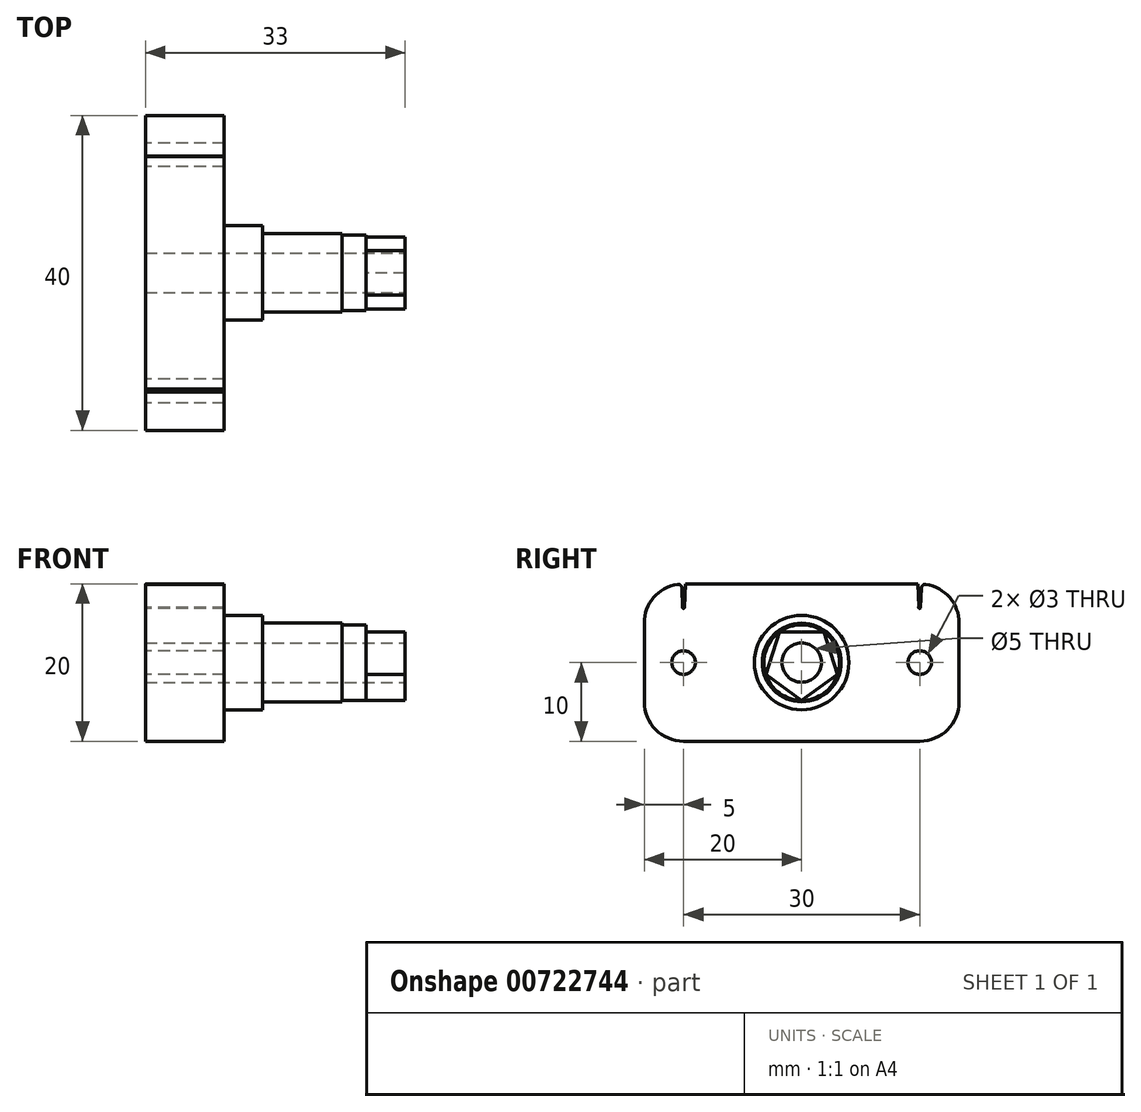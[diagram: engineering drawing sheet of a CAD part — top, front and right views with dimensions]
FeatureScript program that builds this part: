
annotation { "Feature Type Name" : "Feature", "Feature Type Description" : "" }
export const myFeature = defineFeature(function(context is Context, id is Id, definition is map)
    precondition{}
    {
        {
            var Q0;
            Q0=qCreatedBy(makeId("Right.planeOp"),FACE);
            var sketch = newSketch(context, id + "F0", { "sketchPlane" : qUnion([Q0])});
            skCircle(sketch, "E0", {"center": v(0, 0) * mm, "radius": 5 * mm});
            skSolve(sketch);
        }
        {
            var Q0;
            Q0=qSketchRegion(id+"F0",true);
            extrude(context, id + "F1", {"entities" : qUnion([Q0]), "oppositeDirection" : true, "depth" : 25 * mm, "offsetDistance" : 25 * mm});
        }
        {
            var Q0;
            Q0=makeQuery(id+"F1.opExtrude","CAP_FACE",FACE,{"disambiguationData":[OSD([sQuery(id+"F0.wireOp",EDGE,"E0")])],"isStart":true});
            var sketch = newSketch(context, id + "F2", { "sketchPlane" : qUnion([Q0])});
            skCircle(sketch, "E1", {"center": v(0, 0) * mm, "radius": 4.8 * mm});
            skSolve(sketch);
        }
        {
            var Q0;
            Q0=qSketchRegion(id+"F2",true);
            extrude(context, id + "F3", {"entities" : qUnion([Q0]), "operationType" : NewBodyOperationType.ADD, "depth" : 3 * mm, "offsetDistance" : 25 * mm});
        }
        {
            var Q0;
            Q0=makeQuery(id+"F3.opExtrude","CAP_FACE",FACE,{"disambiguationData":[OSD([sQuery(id+"F2.wireOp",EDGE,"E1")])],"isStart":false});
            var sketch = newSketch(context, id + "F4", { "sketchPlane" : qUnion([Q0])});
            skCircle(sketch, "E2.cCircle", {"center": v(0, 0) * mm, "radius": 4.8 * mm, "construction": true});
            skLineSegment(sketch, "E2.0", {"start": v(0, -4.8) * mm, "end": v(-4.57, -1.48) * mm});
            skLineSegment(sketch, "E2.1", {"start": v(-4.57, -1.48) * mm, "end": v(-2.82, 3.88) * mm});
            skLineSegment(sketch, "E2.2", {"start": v(-2.82, 3.88) * mm, "end": v(2.82, 3.88) * mm});
            skLineSegment(sketch, "E2.3", {"start": v(2.82, 3.88) * mm, "end": v(4.57, -1.48) * mm});
            skLineSegment(sketch, "E2.4", {"start": v(4.57, -1.48) * mm, "end": v(0, -4.8) * mm});
            skSolve(sketch);
        }
        {
            var Q0;
            Q0=qSketchRegion(id+"F4",true);
            extrude(context, id + "F5", {"entities" : qUnion([Q0]), "operationType" : NewBodyOperationType.ADD, "depth" : 5 * mm, "offsetDistance" : 25 * mm, "hasSecondDirection" : true, "secondDirectionOppositeDirection" : true, "secondDirectionDepth" : 23 * mm});
        }
        {
            var Q0;
            Q0=makeQuery(id+"F1.opExtrude","CAP_FACE",FACE,{"disambiguationData":[OSD([sQuery(id+"F0.wireOp",EDGE,"E0")])],"isStart":false});
            var sketch = newSketch(context, id + "F6", { "sketchPlane" : qUnion([Q0])});
            skLineSegment(sketch, "E3.bottom", {"start": v(-20, 10) * mm, "end": v(20, 10) * mm});
            skLineSegment(sketch, "E3.top", {"start": v(-20, -10) * mm, "end": v(20, -10) * mm});
            skLineSegment(sketch, "E3.left", {"start": v(-20, 10) * mm, "end": v(-20, -10) * mm});
            skLineSegment(sketch, "E3.right", {"start": v(20, 10) * mm, "end": v(20, -10) * mm});
            skPoint(sketch, "E3.middle", {"position": v(0, 0) * mm});
            skLineSegment(sketch, "E4", {"start": v(0, 0) * mm, "end": v(-15, 0) * mm, "construction": true});
            skLineSegment(sketch, "E5", {"start": v(0, 0) * mm, "end": v(15, 0) * mm});
            skCircle(sketch, "E6", {"center": v(-15, 0) * mm, "radius": 1.5 * mm});
            skCircle(sketch, "E7", {"center": v(15, 0) * mm, "radius": 1.5 * mm});
            skSolve(sketch);
        }
        {
            var Q0;
            Q0 = qSketchRegion(id + "F6", true);
            extrude(context, id + "F7", {"entities" : qUnion([Q0]), "operationType" : NewBodyOperationType.ADD, "oppositeDirection" : true, "depth" : 10 * mm, "offsetDistance" : 25 * mm});
        }
        {
            var Q0;
            Q0=makeQuery(id+"F7.boolean.opBoolean","MERGE",FACE,{"derivedFrom":[makeQuery(id+"F5.opExtrude","CAP_FACE",FACE,{"disambiguationData":[OSD([sQuery(id+"F4.wireOp",EDGE,"E2.0"),sQuery(id+"F4.wireOp",EDGE,"E2.1"),sQuery(id+"F4.wireOp",EDGE,"E2.2"),sQuery(id+"F4.wireOp",EDGE,"E2.3"),sQuery(id+"F4.wireOp",EDGE,"E2.4")])],"isStart":true}),makeQuery(id+"F7.opExtrude","CAP_FACE",FACE,{"disambiguationData":[OSD([sQuery(id+"F6.wireOp",EDGE,"E3.bottom"),sQuery(id+"F6.wireOp",EDGE,"E3.top"),sQuery(id+"F6.wireOp",EDGE,"E3.left"),sQuery(id+"F6.wireOp",EDGE,"E3.right"),sQuery(id+"F6.wireOp",EDGE,"E6"),sQuery(id+"F6.wireOp",EDGE,"E7")])],"isStart":true})]});
            var sketch = newSketch(context, id + "F8", { "sketchPlane" : qUnion([Q0])});
            skLineSegment(sketch, "E8", {"start": v(0, 10) * mm, "end": v(-14.8, 10) * mm, "construction": true});
            skLineSegment(sketch, "E9", {"start": v(-15, 10) * mm, "end": v(-15, 7) * mm, "construction": true});
            skLineSegment(sketch, "E10", {"start": v(-14.8, 10) * mm, "end": v(-15, 10) * mm});
            skLineSegment(sketch, "E11", {"start": v(-15, 10) * mm, "end": v(-14.8, 10) * mm});
            skLineSegment(sketch, "E12", {"start": v(0, 10) * mm, "end": v(15, 10) * mm, "construction": true});
            skLineSegment(sketch, "E13", {"start": v(15, 10) * mm, "end": v(15, 7) * mm, "construction": true});
            skLineSegment(sketch, "E14", {"start": v(14.99, 10) * mm, "end": v(14.74, 10) * mm});
            skLineSegment(sketch, "E15", {"start": v(15.24, 10) * mm, "end": v(15.05, 10) * mm});
            skLineSegment(sketch, "E16", {"start": v(14.99, 10) * mm, "end": v(15.24, 10) * mm});
            skArc(sketch, "E17", {"start": v(14.88, 7) * mm, "mid": v(15.02, 6.88) * mm, "end": v(15.12, 7.03) * mm});
            skLineSegment(sketch, "E18", {"start": v(15.12, 7.03) * mm, "end": v(15.24, 10) * mm});
            skLineSegment(sketch, "E19", {"start": v(14.74, 10) * mm, "end": v(14.88, 7) * mm});
            skLineSegment(sketch, "E20", {"start": v(15.24, 10) * mm, "end": v(14.74, 10) * mm});
            skLineSegment(sketch, "E21", {"start": v(-12.57, 9.9) * mm, "end": v(-12.57, 6.9) * mm, "construction": true});
            skLineSegment(sketch, "E22", {"start": v(-15, 10) * mm, "end": v(-15.25, 10) * mm});
            skLineSegment(sketch, "E23", {"start": v(-14.75, 10) * mm, "end": v(-14.94, 10) * mm});
            skLineSegment(sketch, "E24", {"start": v(-15, 10) * mm, "end": v(-14.75, 10) * mm});
            skArc(sketch, "E25", {"start": v(-15.11, 7) * mm, "mid": v(-14.97, 6.88) * mm, "end": v(-14.86, 7.03) * mm});
            skLineSegment(sketch, "E26", {"start": v(-14.86, 7.03) * mm, "end": v(-14.75, 10) * mm});
            skLineSegment(sketch, "E27", {"start": v(-15.25, 10) * mm, "end": v(-15.11, 7) * mm});
            skLineSegment(sketch, "E28", {"start": v(-14.75, 10) * mm, "end": v(-15.25, 10) * mm});
            skSolve(sketch);
        }
        {
            var Q0;
            Q0 = qSketchRegion(id + "F8", true);
            extrude(context, id + "F9", {"entities" : qUnion([Q0]), "operationType" : NewBodyOperationType.REMOVE, "oppositeDirection" : true, "depth" : 10 * mm, "offsetDistance" : 25 * mm});
        }
        {
            var Q0;
            Q0=makeQuery(id+"F7.opExtrude","SWEPT_EDGE",EDGE,{"disambiguationData":[OSD([sQuery(id+"F6.wireOp",EDGE,"E3.bottom"),sQuery(id+"F6.wireOp",EDGE,"E3.left")])]});
            var Q1;
            Q1=makeQuery(id+"F7.opExtrude","SWEPT_EDGE",EDGE,{"disambiguationData":[OSD([sQuery(id+"F6.wireOp",EDGE,"E3.top"),sQuery(id+"F6.wireOp",EDGE,"E3.left")])]});
            var Q2;
            Q2=makeQuery(id+"F7.opExtrude","SWEPT_EDGE",EDGE,{"disambiguationData":[OSD([sQuery(id+"F6.wireOp",EDGE,"E3.bottom"),sQuery(id+"F6.wireOp",EDGE,"E3.right")])]});
            var Q3;
            Q3=makeQuery(id+"F7.opExtrude","SWEPT_EDGE",EDGE,{"disambiguationData":[OSD([sQuery(id+"F6.wireOp",EDGE,"E3.top"),sQuery(id+"F6.wireOp",EDGE,"E3.right")])]});
            fillet(context, id + "F10", {"entities" : qUnion([Q0, Q1, Q2, Q3]), "radius" : 5 * mm, "tangentPropagation" : true, "allowEdgeOverflow" : false});
        }
        {
            var Q0;
            Q0=makeQuery(id+"F10.opFillet","BLEND_EDGE",EDGE,{"blendedFrom":[makeQuery(id+"F7.opExtrude","SWEPT_EDGE",EDGE,{"disambiguationData":[OSD([sQuery(id+"F6.wireOp",EDGE,"E3.bottom"),sQuery(id+"F6.wireOp",EDGE,"E3.left")])]}),makeQuery(id+"F9.boolean.opBoolean","COPY",FACE,{"derivedFrom":makeQuery(id+"F9.opExtrude","SWEPT_FACE",FACE,{"disambiguationData":[OSD([sQuery(id+"F8.wireOp",EDGE,"j5MYOWD0-buF4-LUkn-qBEQ-IXeojwLEtDlU")])]})})],"blendedInto":[makeQuery(id+"F9.boolean.opBoolean","COPY",FACE,{"derivedFrom":makeQuery(id+"F9.opExtrude","SWEPT_FACE",FACE,{"disambiguationData":[OSD([sQuery(id+"F8.wireOp",EDGE,"j5MYOWD0-buF4-LUkn-qBEQ-IXeojwLEtDlU")])]})})]});
            var Q1;
            Q1=makeQuery(id+"F9.boolean.opBoolean","COPY",EDGE,{"derivedFrom":makeQuery(id+"F9.opExtrude","SWEPT_EDGE",EDGE,{"disambiguationData":[OSD([sQuery(id+"F6.wireOp",EDGE,"E3.bottom"),sQuery(id+"F8.wireOp",EDGE,"w7hy2pTy-gQ0d-KnG3-LhtY-pDF90dZBTLL6"),sQuery(id+"F8.wireOp",EDGE,"E11")])]})});
            var Q2;
            Q2=makeQuery(id+"F10.opFillet","BLEND_EDGE",EDGE,{"blendedFrom":[makeQuery(id+"F7.opExtrude","SWEPT_EDGE",EDGE,{"disambiguationData":[OSD([sQuery(id+"F6.wireOp",EDGE,"E3.bottom"),sQuery(id+"F6.wireOp",EDGE,"E3.right")])]}),makeQuery(id+"F9.boolean.opBoolean","COPY",FACE,{"derivedFrom":makeQuery(id+"F9.opExtrude","SWEPT_FACE",FACE,{"disambiguationData":[OSD([sQuery(id+"F8.wireOp",EDGE,"f21e2cd2-edbb-4066-a94a-ee789b2e384d")])]})})],"blendedInto":[makeQuery(id+"F9.boolean.opBoolean","COPY",FACE,{"derivedFrom":makeQuery(id+"F9.opExtrude","SWEPT_FACE",FACE,{"disambiguationData":[OSD([sQuery(id+"F8.wireOp",EDGE,"f21e2cd2-edbb-4066-a94a-ee789b2e384d")])]})})]});
            var Q3;
            Q3=makeQuery(id+"F9.boolean.opBoolean","COPY",EDGE,{"derivedFrom":makeQuery(id+"F9.opExtrude","SWEPT_EDGE",EDGE,{"disambiguationData":[OSD([sQuery(id+"F6.wireOp",EDGE,"E3.bottom"),sQuery(id+"F8.wireOp",EDGE,"E14"),sQuery(id+"F8.wireOp",EDGE,"db8e2f36-8bb8-4704-858f-84e530f86840")])]})});
            var Q4;
            Q4=makeQuery(id+"F9.boolean.opBoolean","COPY",EDGE,{"derivedFrom":makeQuery(id+"F9.opExtrude","CAP_EDGE",EDGE,{"disambiguationData":[OSD([sQuery(id+"F8.wireOp",EDGE,"j5MYOWD0-buF4-LUkn-qBEQ-IXeojwLEtDlU")])],"isStart":true})});
            var Q5;
            Q5=makeQuery(id+"F9.boolean.opBoolean","COPY",EDGE,{"derivedFrom":makeQuery(id+"F9.opExtrude","CAP_EDGE",EDGE,{"disambiguationData":[OSD([sQuery(id+"F8.wireOp",EDGE,"w7hy2pTy-gQ0d-KnG3-LhtY-pDF90dZBTLL6")])],"isStart":true})});
            var Q6;
            Q6=makeQuery(id+"F9.boolean.opBoolean","COPY",EDGE,{"derivedFrom":makeQuery(id+"F9.opExtrude","CAP_EDGE",EDGE,{"disambiguationData":[OSD([sQuery(id+"F8.wireOp",EDGE,"db8e2f36-8bb8-4704-858f-84e530f86840")])],"isStart":true})});
            var Q7;
            Q7=makeQuery(id+"F9.boolean.opBoolean","COPY",EDGE,{"derivedFrom":makeQuery(id+"F9.opExtrude","CAP_EDGE",EDGE,{"disambiguationData":[OSD([sQuery(id+"F8.wireOp",EDGE,"f21e2cd2-edbb-4066-a94a-ee789b2e384d")])],"isStart":true})});
            var Q8;
            Q8=makeQuery(id+"F9.boolean.opBoolean","COPY",EDGE,{"derivedFrom":makeQuery(id+"F9.opExtrude","SWEPT_EDGE",EDGE,{"disambiguationData":[OSD([sQuery(id+"F8.wireOp",EDGE,"E26"),sQuery(id+"F8.wireOp",EDGE,"E28")])]})});
            var Q9;
            Q9=makeQuery(id+"F10.opFillet","BLEND_EDGE",EDGE,{"blendedFrom":[makeQuery(id+"F7.opExtrude","SWEPT_EDGE",EDGE,{"disambiguationData":[OSD([sQuery(id+"F6.wireOp",EDGE,"E3.bottom"),sQuery(id+"F6.wireOp",EDGE,"E3.left")])]}),makeQuery(id+"F9.boolean.opBoolean","COPY",FACE,{"derivedFrom":makeQuery(id+"F9.opExtrude","SWEPT_FACE",FACE,{"disambiguationData":[OSD([sQuery(id+"F8.wireOp",EDGE,"E27")])]})})],"blendedInto":[makeQuery(id+"F9.boolean.opBoolean","COPY",FACE,{"derivedFrom":makeQuery(id+"F9.opExtrude","SWEPT_FACE",FACE,{"disambiguationData":[OSD([sQuery(id+"F8.wireOp",EDGE,"E27")])]})})]});
            var Q10;
            Q10=makeQuery(id+"F10.opFillet","BLEND_EDGE",EDGE,{"blendedFrom":[makeQuery(id+"F7.opExtrude","SWEPT_EDGE",EDGE,{"disambiguationData":[OSD([sQuery(id+"F6.wireOp",EDGE,"E3.bottom"),sQuery(id+"F6.wireOp",EDGE,"E3.right")])]}),makeQuery(id+"F9.boolean.opBoolean","COPY",FACE,{"derivedFrom":makeQuery(id+"F9.opExtrude","SWEPT_FACE",FACE,{"disambiguationData":[OSD([sQuery(id+"F8.wireOp",EDGE,"E18")])]})})],"blendedInto":[makeQuery(id+"F9.boolean.opBoolean","COPY",FACE,{"derivedFrom":makeQuery(id+"F9.opExtrude","SWEPT_FACE",FACE,{"disambiguationData":[OSD([sQuery(id+"F8.wireOp",EDGE,"E18")])]})})]});
            fillet(context, id + "F11", {"entities" : qUnion([Q0, Q1, Q2, Q3, Q4, Q5, Q6, Q7, Q8, Q9, Q10]), "radius" : 0.5 * mm, "tangentPropagation" : true, "allowEdgeOverflow" : false});
        }
        {
            var Q0;
            Q0=makeQuery(id+"F7.opExtrude","CAP_FACE",FACE,{"disambiguationData":[OSD([sQuery(id+"F6.wireOp",EDGE,"E3.bottom"),sQuery(id+"F6.wireOp",EDGE,"E3.top"),sQuery(id+"F6.wireOp",EDGE,"E3.left"),sQuery(id+"F6.wireOp",EDGE,"E3.right"),sQuery(id+"F6.wireOp",EDGE,"E6"),sQuery(id+"F6.wireOp",EDGE,"E7")])],"isStart":false});
            var sketch = newSketch(context, id + "F12", { "sketchPlane" : qUnion([Q0])});
            skCircle(sketch, "E29", {"center": v(0, 0) * mm, "radius": 6 * mm});
            skSolve(sketch);
        }
        {
            var Q0;
            Q0 = qSketchRegion(id + "F12", true);
            extrude(context, id + "F13", {"entities" : qUnion([Q0]), "operationType" : NewBodyOperationType.ADD, "depth" : 4.9 * mm, "offsetDistance" : 25 * mm});
        }
        {
            var Q0;
            Q0=makeQuery(id+"F5.opExtrude","CAP_FACE",FACE,{"disambiguationData":[OSD([sQuery(id+"F4.wireOp",EDGE,"E2.0"),sQuery(id+"F4.wireOp",EDGE,"E2.1"),sQuery(id+"F4.wireOp",EDGE,"E2.2"),sQuery(id+"F4.wireOp",EDGE,"E2.3"),sQuery(id+"F4.wireOp",EDGE,"E2.4")])],"isStart":false});
            var sketch = newSketch(context, id + "F14", { "sketchPlane" : qUnion([Q0])});
            skCircle(sketch, "E30", {"center": v(0, 0) * mm, "radius": 2.5 * mm});
            skSolve(sketch);
        }
        {
            var Q0;
            Q0=qSketchRegion(id+"F14",true);
            extrude(context, id + "F15", {"entities" : qUnion([Q0]), "operationType" : NewBodyOperationType.REMOVE, "oppositeDirection" : true, "depth" : 65 * mm, "offsetDistance" : 25 * mm});
        }
    });
